# Revit family: 4616 Mesa table
name_source: partatom
category: Furniture
revit_build: Autodesk Revit 2017 (Build: 20171027_0315(x64)
units: mm (PartAtom-declared; Revit-internal decimal feet)

## family parameters
Always vertical = Yes
Cut with Voids When Loaded = No
OmniClass Number = 23.40.20.00
OmniClass Title = General Furniture and Specialties
Room Calculation Point = No
Shared = No
Work Plane-Based = No

## types (3) — shared parameters
Description = With its slim 14 mm tabletop, Mesa is an understated line drawn through the room. The linoleum or laminate tabletop stands in sharp contrast to the soft curves of the aluminium frame and legs.
Design year = 2018
Designer = Welling/Ludvik
Frame = FF Aluminium Black
Gliders = FF Plastic Black
Item No. = 4616
Length = 160 cm
Manufacturer = Fredericia Furniture A/S
Model = Mesa Table
Table Top = FF Linoleum Black
URL = https://www.fredericia.com
Variations Dimensions = Available in special sizes by request
Variations Frame = Available in black or white
Variations Tabletop = Available in black linoleum, white nano laminate or oak veneer lacquered
Weight = 33 kg
Width = 90 cm

## per-type parameters (varying)
| type | Table Height |
| 4616 Mesa table L160xW90xH73 | 730 mm  [stored 2.39501 ft] |
| 4616 Mesa table L160xW90xH96 | 960 mm  [stored 3.14961 ft] |
| 4616 Mesa table L160xW90xH105 | 1050 mm |

note: [stored X ft] marks values corroborated as IEEE doubles in the binary element streams (Revit-internal decimal feet)

## geometry (parser evidence)
native form markers: Sweep x3
no freeform markers — native parametric forms only
